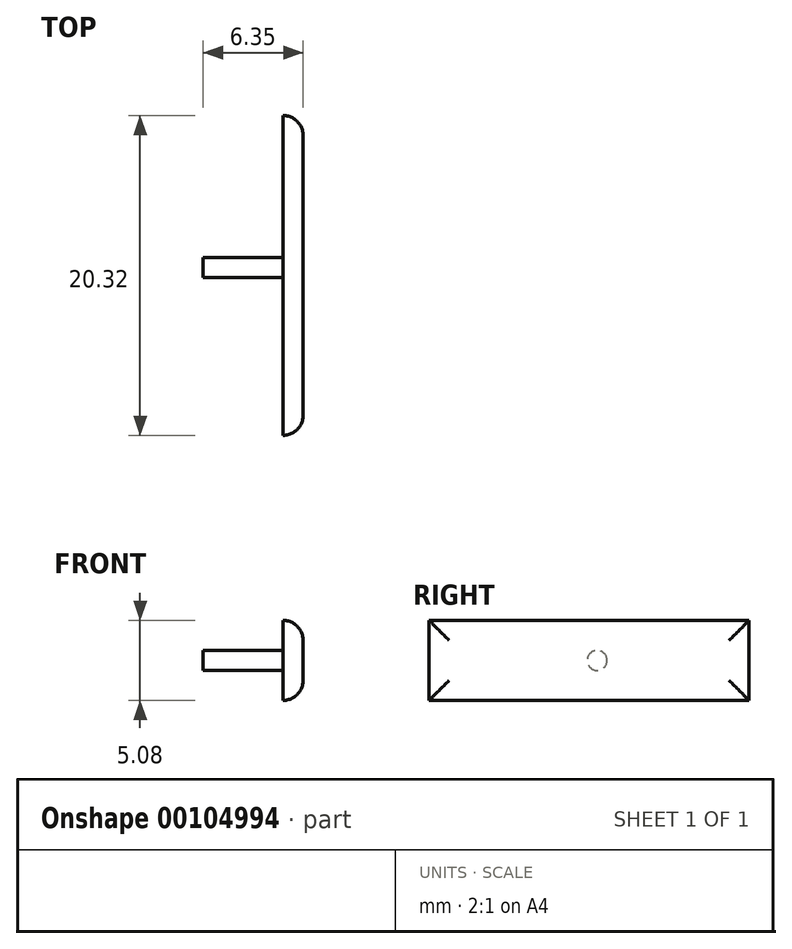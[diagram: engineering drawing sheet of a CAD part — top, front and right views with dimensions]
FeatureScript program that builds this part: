
annotation { "Feature Type Name" : "Feature", "Feature Type Description" : "" }
export const myFeature = defineFeature(function(context is Context, id is Id, definition is map)
    precondition{}
    {
        {
            var Q0;
            Q0=qCreatedBy(makeId("Top.planeOp"),FACE);
            var sketch = newSketch(context, id + "F0", { "sketchPlane" : qUnion([Q0])});
            skLineSegment(sketch, "E0.bottom", {"start": v(0, 9.65) * mm, "end": v(1.27, 9.65) * mm});
            skLineSegment(sketch, "E0.top", {"start": v(0, -10.67) * mm, "end": v(1.27, -10.67) * mm});
            skLineSegment(sketch, "E0.left", {"start": v(0, 9.65) * mm, "end": v(0, -10.67) * mm});
            skLineSegment(sketch, "E0.right", {"start": v(1.27, 9.65) * mm, "end": v(1.27, -10.67) * mm});
            skSolve(sketch);
        }
        {
            var Q0;
            Q0=makeQuery(id+"F0.imprint","IMPRINT",FACE,{"disambiguationData":[TD([[makeQuery(id+"F0.imprint","IMPRINT",EDGE,{"derivedFrom":sQuery(id+"F0.wireOp",EDGE,"E0.bottom")}),-1.0]])]});
            extrude(context, id + "F1", {"entities" : qUnion([Q0]), "depth" : 2.54 * mm, "hasSecondDirection" : true, "secondDirectionOppositeDirection" : true, "secondDirectionDepth" : 2.54 * mm});
        }
        {
            var Q0;
            Q0=makeQuery(id+"F1.opExtrude","SWEPT_EDGE",EDGE,{"disambiguationData":[OSD([sQuery(id+"F0.wireOp",EDGE,"E0.bottom"),sQuery(id+"F0.wireOp",EDGE,"E0.right")])]});
            var Q1;
            Q1=makeQuery(id+"F1.opExtrude","CAP_EDGE",EDGE,{"disambiguationData":[OSD([sQuery(id+"F0.wireOp",EDGE,"E0.right")])],"isStart":false});
            var Q2;
            Q2=makeQuery(id+"F1.opExtrude","CAP_EDGE",EDGE,{"disambiguationData":[OSD([sQuery(id+"F0.wireOp",EDGE,"E0.right")])],"isStart":true});
            var Q3;
            Q3=makeQuery(id+"F1.opExtrude","SWEPT_EDGE",EDGE,{"disambiguationData":[OSD([sQuery(id+"F0.wireOp",EDGE,"E0.top"),sQuery(id+"F0.wireOp",EDGE,"E0.right")])]});
            fillet(context, id + "F2", {"entities" : qUnion([Q0, Q1, Q2, Q3]), "radius" : 1.27 * mm, "tangentPropagation" : true, "allowEdgeOverflow" : false});
        }
        {
            var Q0;
            Q0=makeQuery(id+"F1.opExtrude","SWEPT_FACE",FACE,{"disambiguationData":[OSD([sQuery(id+"F0.wireOp",EDGE,"E0.left")])]});
            var sketch = newSketch(context, id + "F3", { "sketchPlane" : qUnion([Q0])});
            skCircle(sketch, "E1", {"center": v(0, 0) * mm, "radius": 0.64 * mm});
            skSolve(sketch);
        }
        {
            var Q0;
            Q0=makeQuery(id+"F3.imprint","IMPRINT",FACE,{"disambiguationData":[TD([[makeQuery(id+"F3.imprint","IMPRINT",EDGE,{"derivedFrom":sQuery(id+"F3.wireOp",EDGE,"E1")}),1.0]])]});
            extrude(context, id + "F4", {"entities" : qUnion([Q0]), "operationType" : NewBodyOperationType.ADD, "depth" : 5.08 * mm});
        }
    });
